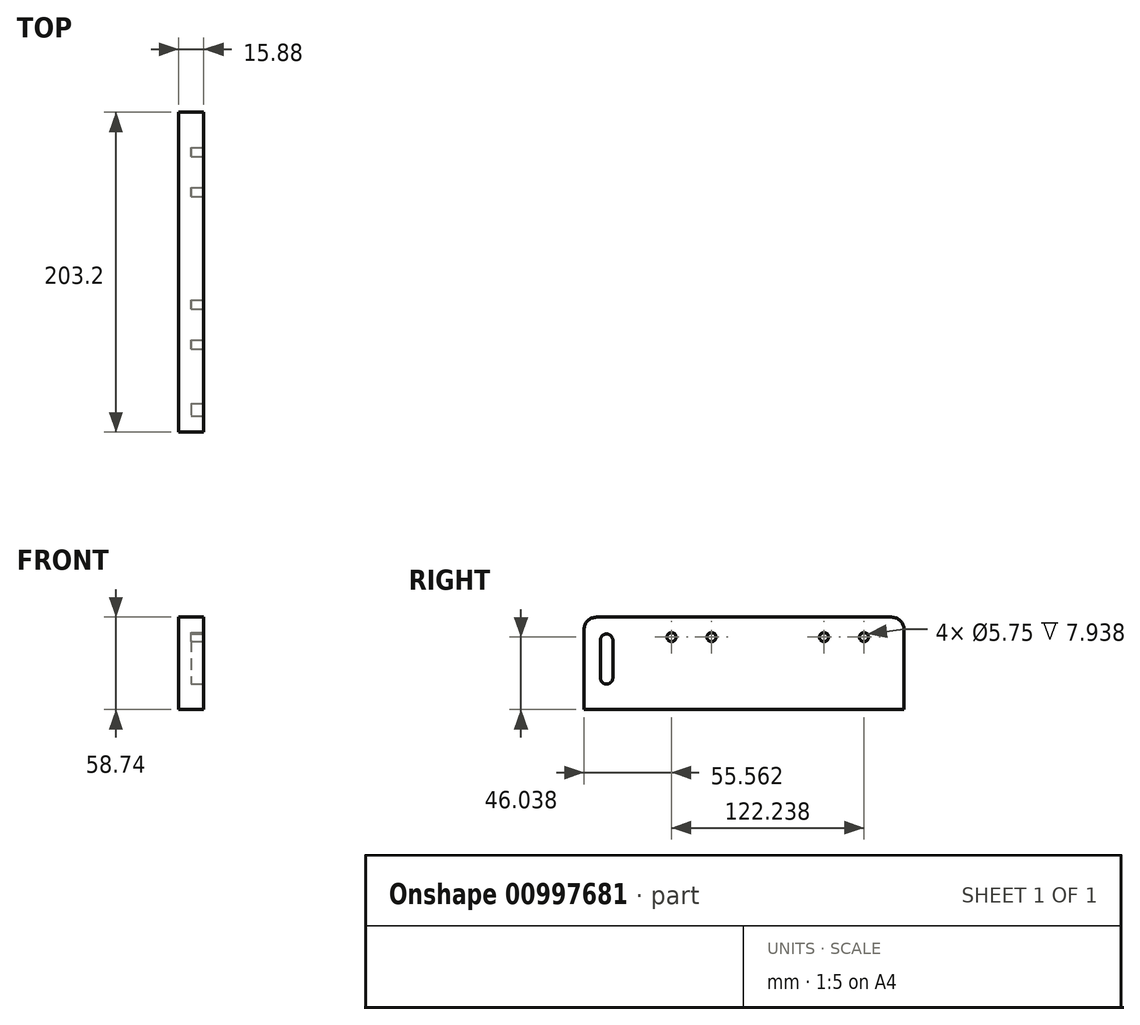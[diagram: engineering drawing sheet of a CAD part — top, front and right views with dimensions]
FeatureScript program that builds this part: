
annotation { "Feature Type Name" : "Feature", "Feature Type Description" : "" }
export const myFeature = defineFeature(function(context is Context, id is Id, definition is map)
    precondition{}
    {
        {
            var Q0;
            Q0=qCreatedBy(makeId("Right.planeOp"),FACE);
            var sketch = newSketch(context, id + "F0", { "sketchPlane" : qUnion([Q0])});
            skLineSegment(sketch, "E0", {"start": v(0, 0) * mm, "end": v(203.2, 0) * mm});
            skLineSegment(sketch, "E1", {"start": v(203.2, 0) * mm, "end": v(203.2, 50.8) * mm});
            skLineSegment(sketch, "E2", {"start": v(195.26, 58.74) * mm, "end": v(7.94, 58.74) * mm});
            skLineSegment(sketch, "E3", {"start": v(0, 50.8) * mm, "end": v(0, 0) * mm});
            skPoint(sketch, "E4.visualSharp", {"position": v(0, 58.74) * mm});
            skArc(sketch, "E4.filletArc", {"start": v(7.94, 58.74) * mm, "mid": v(2.32, 56.41) * mm, "end": v(0, 50.8) * mm});
            skPoint(sketch, "E5.visualSharp", {"position": v(203.2, 58.74) * mm});
            skArc(sketch, "E5.filletArc", {"start": v(203.2, 50.8) * mm, "mid": v(200.88, 56.41) * mm, "end": v(195.26, 58.74) * mm});
            skSolve(sketch);
        }
        {
            var Q0;
            Q0 = qSketchRegion(id + "F0", true);
            extrude(context, id + "F1", {"entities" : qUnion([Q0]), "depth" : 15.88 * mm, "offsetDistance" : 25.4 * mm});
        }
        {
            var Q0;
            Q0=makeQuery(id+"F1.opExtrude","CAP_FACE",FACE,{"disambiguationData":[OSD([sQuery(id+"F0.wireOp",EDGE,"E0"),sQuery(id+"F0.wireOp",EDGE,"E1"),sQuery(id+"F0.wireOp",EDGE,"E2"),sQuery(id+"F0.wireOp",EDGE,"E3"),sQuery(id+"F0.wireOp",EDGE,"E4.filletArc"),sQuery(id+"F0.wireOp",EDGE,"E5.filletArc")])],"isStart":false});
            var sketch = newSketch(context, id + "F2", { "sketchPlane" : qUnion([Q0])});
            skLineSegment(sketch, "E6", {"start": v(10.32, 44.05) * mm, "end": v(10.32, 20.24) * mm});
            skArc(sketch, "E7", {"start": v(18.26, 44.05) * mm, "mid": v(14.29, 48.02) * mm, "end": v(10.32, 44.05) * mm});
            skArc(sketch, "E8", {"start": v(10.32, 20.24) * mm, "mid": v(14.29, 16.27) * mm, "end": v(18.26, 20.24) * mm});
            skLineSegment(sketch, "E9", {"start": v(18.26, 44.05) * mm, "end": v(18.26, 20.24) * mm});
            skPoint(sketch, "E10.endSnap0", {"position": v(14.29, 16.27) * mm});
            skPoint(sketch, "E11.endSnap0", {"position": v(14.29, 48.02) * mm});
            skLineSegment(sketch, "E12", {"start": v(0, 5.56) * mm, "end": v(203.2, 5.56) * mm, "construction": true});
            skLineSegment(sketch, "E13", {"start": v(14.29, 16.27) * mm, "end": v(14.29, 5.56) * mm, "construction": true});
            skLineSegment(sketch, "E14", {"start": v(14.29, 48.02) * mm, "end": v(14.29, 58.74) * mm, "construction": true});
            skCircle(sketch, "E15", {"center": v(55.56, 46.04) * mm, "radius": 2.88 * mm});
            skCircle(sketch, "E16", {"center": v(80.96, 46.04) * mm, "radius": 2.88 * mm});
            skCircle(sketch, "E17", {"center": v(152.4, 46.04) * mm, "radius": 2.88 * mm});
            skCircle(sketch, "E18", {"center": v(177.8, 46.04) * mm, "radius": 2.88 * mm});
            skLineSegment(sketch, "E19", {"start": v(55.56, 46.04) * mm, "end": v(80.96, 46.04) * mm, "construction": true});
            skLineSegment(sketch, "E20", {"start": v(152.4, 46.04) * mm, "end": v(177.8, 46.04) * mm, "construction": true});
            skLineSegment(sketch, "E21", {"start": v(80.96, 46.04) * mm, "end": v(152.4, 46.04) * mm, "construction": true});
            skSolve(sketch);
        }
        {
            var Q0;
            Q0 = qSketchRegion(id + "F2", true);
            extrude(context, id + "F3", {"entities" : qUnion([Q0]), "operationType" : NewBodyOperationType.REMOVE, "oppositeDirection" : true, "depth" : 7.94 * mm, "offsetDistance" : 25.4 * mm});
        }
    });
